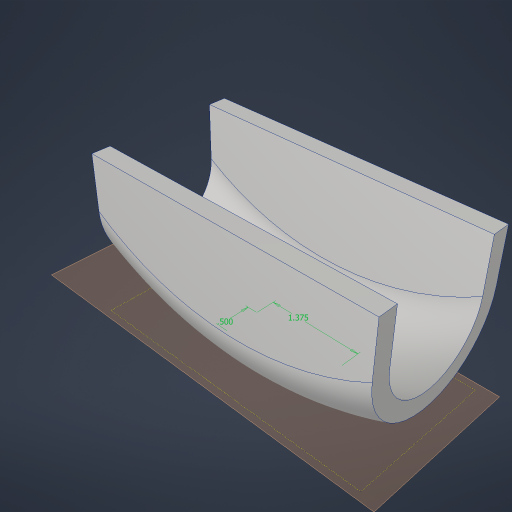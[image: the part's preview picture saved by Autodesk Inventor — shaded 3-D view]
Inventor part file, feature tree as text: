
AUTODESK INVENTOR PART (.ipt)
format: ipt  version: 2023.4 (Build 274418000, 418)  size: 286,208 bytes
history: native  units: in
note: dims shown in document units (in); Inventor stores cm internally (conversion verified against a paired STEP export)
features: sketch x5, projected_geometry x4, extrude x2, sweep x2, plane x1
ambient origin geometry x8: Origin, YZ Plane, XZ Plane, XY Plane, X Axis, Y Axis, Z Axis, Center Point
bodies: Solid1 (feature_tree)
feature tree (14):
  extrude  "Extrusion1"  Depth=2.5in
  sketch  "Sketch2"  dims[d2=2.0in d3=0.0in d4=1.5in]
  sketch  "Sketch3"  dims[d5=3.75in d6=0.0in d7=0.0in]
  sweep  "Sweep1"
  extrude  "Extrusion2"  TaperAngle=0.0deg  [1 undecoded]
  sweep  "Sweep3"
  plane  "Work Plane1"
  sketch  "Sketch6"  dims[d14=0.0in d15=0.0in d16=0.5in d17=1.375in]
  sketch  "Sketch1"  dims[d0=4.0in d1=2.5in]
  sketch  "Sketch5"  dims[d8=0.0in d9=0.0in d13=0.25in]
  projected_geometry  "Projected Loop1"
  projected_geometry  "Project Cut Edges1"
  projected_geometry  "Project Cut Edges2"
  projected_geometry  "Project Cut Edges5"
note: 1 required parameter value undecoded (feature->parameter linkage not recoverable at this tier; creation-order binding heuristic only, values carry confidence <= 0.55)
